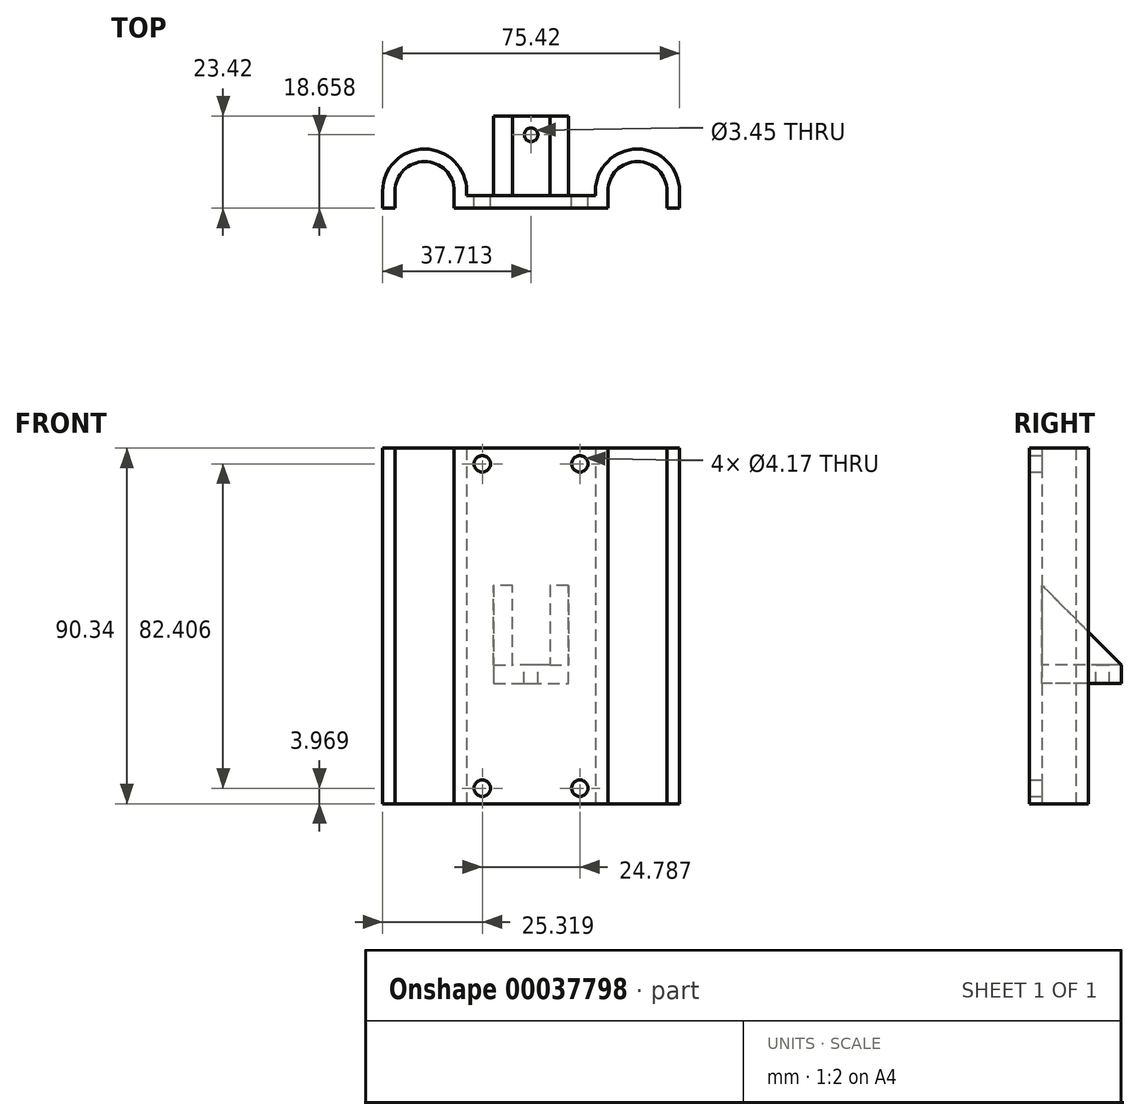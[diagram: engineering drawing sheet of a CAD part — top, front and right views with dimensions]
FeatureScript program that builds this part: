
annotation { "Feature Type Name" : "Feature", "Feature Type Description" : "" }
export const myFeature = defineFeature(function(context is Context, id is Id, definition is map)
    precondition{}
    {
        {
            var Q0;
            Q0=qCreatedBy(makeId("Top.planeOp"),FACE);
            var sketch = newSketch(context, id + "F0", { "sketchPlane" : qUnion([Q0])});
            skLineSegment(sketch, "E0.bottom", {"start": v(0, 0) * mm, "end": v(32.72, 0) * mm});
            skLineSegment(sketch, "E0.top", {"start": v(-3.18, -3.17) * mm, "end": v(35.9, -3.17) * mm});
            skLineSegment(sketch, "E1", {"start": v(16.36, 0) * mm, "end": v(16.36, -3.18) * mm, "construction": true});
            skLineSegment(sketch, "E2", {"start": v(0, 1.15) * mm, "end": v(-3.18, 1.15) * mm, "construction": true});
            skLineSegment(sketch, "E3", {"start": v(32.72, 1.15) * mm, "end": v(35.9, 1.15) * mm, "construction": true});
            skLineSegment(sketch, "E4", {"start": v(35.9, 1.15) * mm, "end": v(50.9, 1.15) * mm, "construction": true});
            skLineSegment(sketch, "E5", {"start": v(-3.18, 1.15) * mm, "end": v(-18.18, 1.15) * mm, "construction": true});
            skLineSegment(sketch, "E6", {"start": v(32.72, 0) * mm, "end": v(32.72, 1.15) * mm});
            skLineSegment(sketch, "E7", {"start": v(35.9, 1.15) * mm, "end": v(35.9, -3.18) * mm});
            skLineSegment(sketch, "E8", {"start": v(50.9, 1.15) * mm, "end": v(54.07, 1.15) * mm, "construction": true});
            skLineSegment(sketch, "E9", {"start": v(-18.18, 1.15) * mm, "end": v(-21.35, 1.15) * mm, "construction": true});
            skLineSegment(sketch, "E10", {"start": v(-3.18, 1.15) * mm, "end": v(-3.18, -3.17) * mm});
            skLineSegment(sketch, "E11", {"start": v(0, 1.15) * mm, "end": v(0, 0) * mm});
            skArc(sketch, "E12", {"start": v(0, 1.15) * mm, "mid": v(-10.67, 11.83) * mm, "end": v(-21.35, 1.15) * mm});
            skArc(sketch, "E13", {"start": v(54.07, 1.15) * mm, "mid": v(43.4, 11.83) * mm, "end": v(32.72, 1.15) * mm});
            skArc(sketch, "E14", {"start": v(50.9, 1.15) * mm, "mid": v(43.4, 8.65) * mm, "end": v(35.9, 1.15) * mm});
            skArc(sketch, "E15", {"start": v(-3.18, 1.15) * mm, "mid": v(-10.67, 8.65) * mm, "end": v(-18.17, 1.15) * mm});
            skLineSegment(sketch, "E16.bottom", {"start": v(54.07, -3.18) * mm, "end": v(50.9, -3.18) * mm});
            skLineSegment(sketch, "E16.left", {"start": v(54.07, -3.18) * mm, "end": v(54.07, 1.15) * mm});
            skLineSegment(sketch, "E16.right", {"start": v(50.9, -3.18) * mm, "end": v(50.9, 1.15) * mm});
            skLineSegment(sketch, "E17.top", {"start": v(-18.18, -3.18) * mm, "end": v(-21.35, -3.18) * mm});
            skLineSegment(sketch, "E17.left", {"start": v(-18.18, 1.15) * mm, "end": v(-18.18, -3.18) * mm});
            skLineSegment(sketch, "E17.right", {"start": v(-21.35, 1.15) * mm, "end": v(-21.35, -3.18) * mm});
            skSolve(sketch);
        }
        {
            var Q0;
            Q0 = qSketchRegion(id + "F0", true);
            extrude(context, id + "F1", {"entities" : qUnion([Q0]), "depth" : 90.34 * mm});
        }
        {
            var Q0;
            Q0=makeQuery(id+"F1.opExtrude","SWEPT_FACE",FACE,{"disambiguationData":[OSD([sQuery(id+"F0.wireOp",EDGE,"E0.bottom")])]});
            var sketch = newSketch(context, id + "F2", { "sketchPlane" : qUnion([Q0])});
            skLineSegment(sketch, "E18", {"start": v(-16.36, 0) * mm, "end": v(-16.36, 90.34) * mm, "construction": true});
            skLineSegment(sketch, "E19.rect.bottom", {"start": v(-28.76, 3.97) * mm, "end": v(-3.97, 3.97) * mm, "construction": true});
            skLineSegment(sketch, "E19.rect.top", {"start": v(-28.76, 86.38) * mm, "end": v(-3.97, 86.38) * mm, "construction": true});
            skLineSegment(sketch, "E19.rect.left", {"start": v(-28.76, 3.97) * mm, "end": v(-28.76, 86.38) * mm, "construction": true});
            skLineSegment(sketch, "E19.rect.right", {"start": v(-3.97, 3.97) * mm, "end": v(-3.97, 86.38) * mm, "construction": true});
            skPoint(sketch, "E19.rect.middle", {"position": v(-16.36, 45.17) * mm});
            skLineSegment(sketch, "E20.bottom", {"start": v(-28.76, 3.97) * mm, "end": v(-32.72, 3.97) * mm, "construction": true});
            skLineSegment(sketch, "E20.top", {"start": v(-28.76, 0) * mm, "end": v(-32.72, 0) * mm, "construction": true});
            skLineSegment(sketch, "E20.left", {"start": v(-28.76, 3.97) * mm, "end": v(-28.76, 0) * mm, "construction": true});
            skLineSegment(sketch, "E20.right", {"start": v(-32.72, 3.97) * mm, "end": v(-32.72, 0) * mm, "construction": true});
            skCircle(sketch, "E21", {"center": v(-3.97, 3.97) * mm, "radius": 2.08 * mm});
            skCircle(sketch, "E22", {"center": v(-28.76, 3.97) * mm, "radius": 2.08 * mm});
            skCircle(sketch, "E23", {"center": v(-28.76, 86.38) * mm, "radius": 2.08 * mm});
            skCircle(sketch, "E24", {"center": v(-3.97, 86.38) * mm, "radius": 2.08 * mm});
            skSolve(sketch);
        }
        {
            var Q0;
            Q0 = qSketchRegion(id + "F2", true);
            var Q1;
            Q1=makeQuery(id+"F1.opExtrude","SWEPT_FACE",FACE,{"disambiguationData":[OSD([sQuery(id+"F0.wireOp",EDGE,"E0.top")])]});
            extrude(context, id + "F3", {"entities" : qUnion([Q0]), "operationType" : NewBodyOperationType.REMOVE, "endBound" : BoundingType.UP_TO_SURFACE, "oppositeDirection" : true, "endBoundEntityFace" : qUnion([Q1]), "depth" : 25.4 * mm});
        }
        {
            var Q0;
            Q0=makeQuery(id+"F1.opExtrude","SWEPT_FACE",FACE,{"disambiguationData":[OSD([sQuery(id+"F0.wireOp",EDGE,"E0.bottom")])]});
            var sketch = newSketch(context, id + "F4", { "sketchPlane" : qUnion([Q0])});
            skLineSegment(sketch, "E25", {"start": v(-25.89, 30.53) * mm, "end": v(-25.89, 55.53) * mm});
            skLineSegment(sketch, "E26", {"start": v(-25.89, 55.53) * mm, "end": v(-21.12, 55.53) * mm});
            skLineSegment(sketch, "E27", {"start": v(-21.12, 55.53) * mm, "end": v(-21.12, 35.29) * mm});
            skLineSegment(sketch, "E28", {"start": v(-21.12, 35.29) * mm, "end": v(-11.6, 35.29) * mm});
            skLineSegment(sketch, "E29", {"start": v(-11.6, 35.29) * mm, "end": v(-11.6, 55.53) * mm});
            skLineSegment(sketch, "E30", {"start": v(-11.6, 55.53) * mm, "end": v(-6.84, 55.53) * mm});
            skLineSegment(sketch, "E31", {"start": v(-6.84, 55.53) * mm, "end": v(-6.84, 30.53) * mm});
            skLineSegment(sketch, "E32", {"start": v(-6.84, 30.53) * mm, "end": v(-25.89, 30.53) * mm});
            skLineSegment(sketch, "E33", {"start": v(-16.36, 30.53) * mm, "end": v(-16.36, 0) * mm, "construction": true});
            skSolve(sketch);
        }
        {
            var Q0;
            Q0 = qSketchRegion(id + "F4", true);
            extrude(context, id + "F5", {"entities" : qUnion([Q0]), "operationType" : NewBodyOperationType.ADD, "depth" : 20.24 * mm});
        }
        {
            var Q0;
            Q0=makeQuery(id+"F5.opExtrude","CAP_EDGE",EDGE,{"disambiguationData":[OSD([sQuery(id+"F4.wireOp",EDGE,"E26")])],"isStart":false});
            var Q1;
            Q1=makeQuery(id+"F5.opExtrude","CAP_EDGE",EDGE,{"disambiguationData":[OSD([sQuery(id+"F4.wireOp",EDGE,"E30")])],"isStart":false});
            chamfer(context, id + "F6", {"entities" : qUnion([Q0, Q1]), "width" : 20.24 * mm, "tangentPropagation" : true});
        }
        {
            var Q0;
            Q0=makeQuery(id+"F5.opExtrude","SWEPT_FACE",FACE,{"disambiguationData":[OSD([sQuery(id+"F4.wireOp",EDGE,"E28")])]});
            var sketch = newSketch(context, id + "F7", { "sketchPlane" : qUnion([Q0])});
            skLineSegment(sketch, "E34", {"start": v(16.36, 15.48) * mm, "end": v(21.12, 15.48) * mm, "construction": true});
            skCircle(sketch, "E35", {"center": v(16.36, 15.48) * mm, "radius": 1.73 * mm});
            skLineSegment(sketch, "E36", {"start": v(16.36, 15.48) * mm, "end": v(16.36, 20.24) * mm, "construction": true});
            skSolve(sketch);
        }
        {
            var Q0;
            Q0 = qSketchRegion(id + "F7", true);
            var Q1;
            Q1=makeQuery(id+"F5.boolean.opBoolean","MERGE",FACE,{"derivedFrom":[makeQuery(id+"FdqMiX9iAEwRQgD_1.boolean.opBoolean","COPY",FACE,{"derivedFrom":makeQuery(id+"FdqMiX9iAEwRQgD_1.opExtrude","SWEPT_FACE",FACE,{"disambiguationData":[OSD([sQuery(id+"FZwneDaGpjM3VRp_1.wireOp",EDGE,"4ee54423-1537-4370-891b-478678dd25e2.bottom")])]})}),makeQuery(id+"F5.opExtrude","SWEPT_FACE",FACE,{"disambiguationData":[OSD([sQuery(id+"F4.wireOp",EDGE,"E32")])]})]});
            extrude(context, id + "F8", {"entities" : qUnion([Q0]), "operationType" : NewBodyOperationType.REMOVE, "endBound" : BoundingType.UP_TO_SURFACE, "oppositeDirection" : true, "endBoundEntityFace" : qUnion([Q1]), "depth" : 25.4 * mm});
        }
    });
